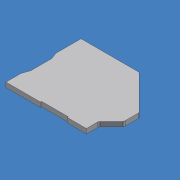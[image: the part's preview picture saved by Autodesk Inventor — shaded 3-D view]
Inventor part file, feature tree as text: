
AUTODESK INVENTOR PART (.ipt)
format: ipt  version: unknown  size: 173,056 bytes
history: native  units: mm (DEFAULTED — no unit token found)
features: extrude x1, sketch x1
ambient origin geometry x8: Origin, YZ Plane, XZ Plane, XY Plane, X Axis, Y Axis, Z Axis, Center Point
feature tree (2):
  extrude  "Extrusion1"  [1 undecoded]
  sketch  "Skizze_1"  dims[d0=1.7mm d1=0.0mm]
note: 1 required parameter value undecoded (feature->parameter linkage not recoverable at this tier; creation-order binding heuristic only, values carry confidence <= 0.55)
